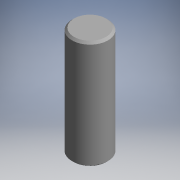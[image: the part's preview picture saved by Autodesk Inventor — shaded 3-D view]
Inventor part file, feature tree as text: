
AUTODESK INVENTOR PART (.ipt)
format: ipt  version: 2017.3 (Build 213256000, 256)  size: 97,792 bytes
history: native  units: mm (DEFAULTED — no unit token found)
features: other x35, revolve x1, sketch x1
ambient origin geometry x8: Origin, YZ Plane, XZ Plane, XY Plane, X Axis, Y Axis, Z Axis, Center Point
bodies: Solid1 (feature_tree)
feature tree (37):
  revolve  "Revolution1"  [1 undecoded]
  other  "dia1_XY"
  other  "dia1_YZ"
  other  "dia1_ZX"
  other  "dia1_X"
  other  "dia1_Y"
  other  "dia1_Z"
  other  "dia1_Center"
  other  "dia2_XY"
  other  "dia2_YZ"
  other  "dia2_ZX"
  other  "dia2_X"
  other  "dia2_Y"
  other  "dia2_Z"
  other  "dia2_Center"
  other  "pin_XY"
  other  "pin_YZ"
  other  "pin_ZX"
  other  "pin_X"
  other  "pin_Y"
  other  "pin_Z"
  other  "pin_Center"
  other  "pin1_XY"
  other  "pin1_YZ"
  other  "pin1_ZX"
  other  "pin1_X"
  other  "pin1_Y"
  other  "pin1_Z"
  other  "pin1_Center"
  other  "pin2_XY"
  other  "pin2_YZ"
  other  "pin2_ZX"
  other  "pin2_X"
  other  "pin2_Y"
  other  "pin2_Z"
  other  "pin2_Center"
  sketch  "Sketch_1"  dims[d0=360.0deg]
note: 1 required parameter value undecoded (feature->parameter linkage not recoverable at this tier; creation-order binding heuristic only, values carry confidence <= 0.55)
